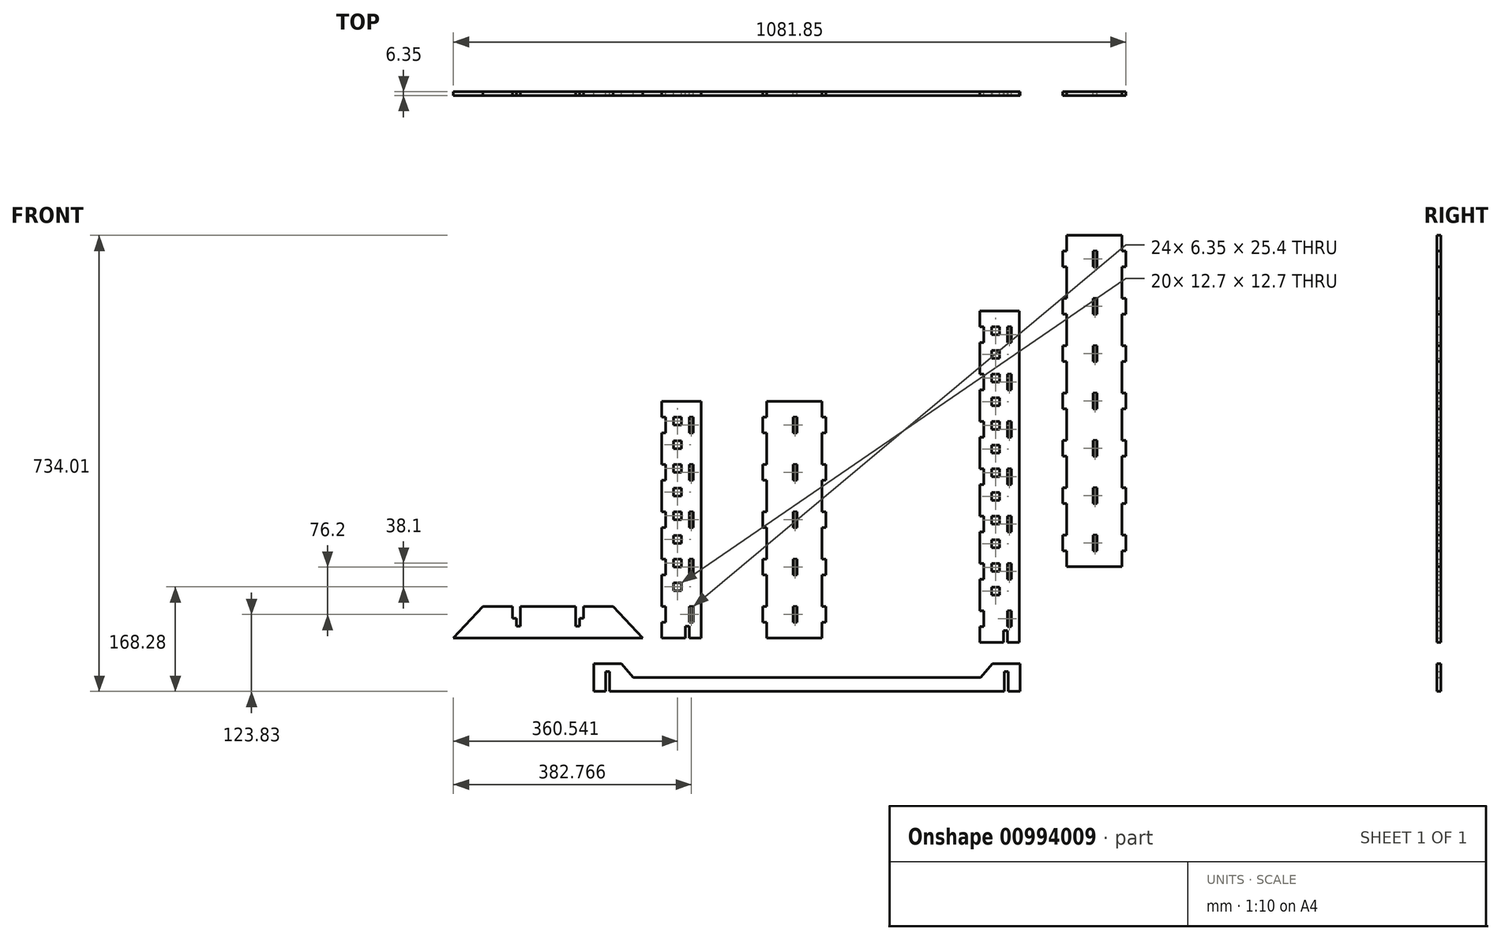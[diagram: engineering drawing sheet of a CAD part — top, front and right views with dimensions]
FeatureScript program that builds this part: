
annotation { "Feature Type Name" : "Feature", "Feature Type Description" : "" }
export const myFeature = defineFeature(function(context is Context, id is Id, definition is map)
    precondition{}
    {
        {
            var Q0;
            Q0=qCreatedBy(makeId("Front.planeOp"),FACE);
            var sketch = newSketch(context, id + "F0", { "sketchPlane" : qUnion([Q0])});
            skLineSegment(sketch, "E0", {"start": v(43.26, 355.6) * mm, "end": v(49.61, 355.6) * mm});
            skLineSegment(sketch, "E1", {"start": v(43.26, 330.2) * mm, "end": v(49.61, 330.2) * mm});
            skLineSegment(sketch, "E2", {"start": v(43.26, 279.4) * mm, "end": v(49.61, 279.4) * mm});
            skLineSegment(sketch, "E3", {"start": v(43.26, 254) * mm, "end": v(49.61, 254) * mm});
            skLineSegment(sketch, "E4", {"start": v(43.26, 203.2) * mm, "end": v(49.61, 203.2) * mm});
            skLineSegment(sketch, "E5", {"start": v(43.26, 177.8) * mm, "end": v(49.61, 177.8) * mm});
            skLineSegment(sketch, "E6", {"start": v(43.26, 127) * mm, "end": v(49.61, 127) * mm});
            skLineSegment(sketch, "E7", {"start": v(43.26, 101.6) * mm, "end": v(49.61, 101.6) * mm});
            skLineSegment(sketch, "E8", {"start": v(43.26, 50.8) * mm, "end": v(49.61, 50.8) * mm});
            skLineSegment(sketch, "E9", {"start": v(43.26, 25.4) * mm, "end": v(49.61, 25.4) * mm});
            skLineSegment(sketch, "E10", {"start": v(43.26, 0) * mm, "end": v(43.26, 25.4) * mm});
            skLineSegment(sketch, "E11", {"start": v(49.61, 25.4) * mm, "end": v(49.61, 50.8) * mm});
            skLineSegment(sketch, "E12", {"start": v(43.26, 50.8) * mm, "end": v(43.26, 101.6) * mm});
            skLineSegment(sketch, "E13", {"start": v(49.61, 101.6) * mm, "end": v(49.61, 127) * mm});
            skLineSegment(sketch, "E14", {"start": v(43.26, 127) * mm, "end": v(43.26, 177.8) * mm});
            skLineSegment(sketch, "E15", {"start": v(49.61, 177.8) * mm, "end": v(49.61, 203.2) * mm});
            skLineSegment(sketch, "E16", {"start": v(43.26, 203.2) * mm, "end": v(43.26, 254) * mm});
            skLineSegment(sketch, "E17", {"start": v(49.61, 254) * mm, "end": v(49.61, 279.4) * mm});
            skLineSegment(sketch, "E18", {"start": v(43.26, 279.4) * mm, "end": v(43.26, 330.2) * mm});
            skLineSegment(sketch, "E19", {"start": v(49.61, 330.2) * mm, "end": v(49.61, 355.6) * mm});
            skLineSegment(sketch, "E20", {"start": v(43.26, 355.6) * mm, "end": v(43.26, 381) * mm});
            skLineSegment(sketch, "E21", {"start": v(-45.64, 0) * mm, "end": v(43.26, 0) * mm});
            skLineSegment(sketch, "E22", {"start": v(-45.64, 381) * mm, "end": v(43.26, 381) * mm});
            skLineSegment(sketch, "E23", {"start": v(-45.64, 25.4) * mm, "end": v(-51.99, 25.4) * mm});
            skLineSegment(sketch, "E24", {"start": v(-45.64, 50.8) * mm, "end": v(-51.99, 50.8) * mm});
            skLineSegment(sketch, "E25", {"start": v(-45.64, 101.6) * mm, "end": v(-51.99, 101.6) * mm});
            skLineSegment(sketch, "E26", {"start": v(-45.64, 127) * mm, "end": v(-51.99, 127) * mm});
            skLineSegment(sketch, "E27", {"start": v(-45.64, 177.8) * mm, "end": v(-51.99, 177.8) * mm});
            skLineSegment(sketch, "E28", {"start": v(-45.64, 203.2) * mm, "end": v(-51.99, 203.2) * mm});
            skLineSegment(sketch, "E29", {"start": v(-45.64, 254) * mm, "end": v(-51.99, 254) * mm});
            skLineSegment(sketch, "E30", {"start": v(-45.64, 279.4) * mm, "end": v(-51.99, 279.4) * mm});
            skLineSegment(sketch, "E31", {"start": v(-45.64, 330.2) * mm, "end": v(-51.99, 330.2) * mm});
            skLineSegment(sketch, "E32", {"start": v(-45.64, 355.6) * mm, "end": v(-51.99, 355.6) * mm});
            skLineSegment(sketch, "E33", {"start": v(-45.64, 381) * mm, "end": v(-45.64, 355.6) * mm});
            skLineSegment(sketch, "E34", {"start": v(-45.64, 330.2) * mm, "end": v(-45.64, 279.4) * mm});
            skLineSegment(sketch, "E35", {"start": v(-51.99, 279.4) * mm, "end": v(-51.99, 254) * mm});
            skLineSegment(sketch, "E36", {"start": v(-45.64, 254) * mm, "end": v(-45.64, 203.2) * mm});
            skLineSegment(sketch, "E37", {"start": v(-51.99, 203.2) * mm, "end": v(-51.99, 177.8) * mm});
            skLineSegment(sketch, "E38", {"start": v(-45.64, 177.8) * mm, "end": v(-45.64, 127) * mm});
            skLineSegment(sketch, "E39", {"start": v(-51.99, 127) * mm, "end": v(-51.99, 101.6) * mm});
            skLineSegment(sketch, "E40", {"start": v(-45.64, 101.6) * mm, "end": v(-45.64, 50.8) * mm});
            skLineSegment(sketch, "E41", {"start": v(-51.99, 50.8) * mm, "end": v(-51.99, 25.4) * mm});
            skLineSegment(sketch, "E42", {"start": v(-45.64, 25.4) * mm, "end": v(-45.64, 0) * mm});
            skLineSegment(sketch, "E43", {"start": v(-51.99, 355.6) * mm, "end": v(-51.99, 330.2) * mm});
            skLineSegment(sketch, "E44", {"start": v(2.99, 25.4) * mm, "end": v(-3.36, 25.4) * mm});
            skLineSegment(sketch, "E45", {"start": v(2.99, 50.8) * mm, "end": v(-3.36, 50.8) * mm});
            skLineSegment(sketch, "E46", {"start": v(2.99, 101.6) * mm, "end": v(-3.36, 101.6) * mm});
            skLineSegment(sketch, "E47", {"start": v(2.99, 127) * mm, "end": v(-3.36, 127) * mm});
            skLineSegment(sketch, "E48", {"start": v(2.99, 177.8) * mm, "end": v(-3.36, 177.8) * mm});
            skLineSegment(sketch, "E49", {"start": v(2.99, 203.2) * mm, "end": v(-3.36, 203.2) * mm});
            skLineSegment(sketch, "E50", {"start": v(2.99, 254) * mm, "end": v(-3.36, 254) * mm});
            skLineSegment(sketch, "E51", {"start": v(2.99, 279.4) * mm, "end": v(-3.36, 279.4) * mm});
            skLineSegment(sketch, "E52", {"start": v(2.99, 330.2) * mm, "end": v(-3.36, 330.2) * mm});
            skLineSegment(sketch, "E53", {"start": v(2.99, 355.6) * mm, "end": v(-3.36, 355.6) * mm});
            skLineSegment(sketch, "E54", {"start": v(-3.36, 279.4) * mm, "end": v(-3.36, 254) * mm});
            skLineSegment(sketch, "E55", {"start": v(-3.36, 203.2) * mm, "end": v(-3.36, 177.8) * mm});
            skLineSegment(sketch, "E56", {"start": v(-3.36, 127) * mm, "end": v(-3.36, 101.6) * mm});
            skLineSegment(sketch, "E57", {"start": v(-3.36, 50.8) * mm, "end": v(-3.36, 25.4) * mm});
            skLineSegment(sketch, "E58", {"start": v(-3.36, 355.6) * mm, "end": v(-3.36, 330.2) * mm});
            skLineSegment(sketch, "E59", {"start": v(2.99, 355.6) * mm, "end": v(2.99, 330.2) * mm});
            skLineSegment(sketch, "E60", {"start": v(2.99, 279.4) * mm, "end": v(2.99, 254) * mm});
            skLineSegment(sketch, "E61", {"start": v(2.99, 203.2) * mm, "end": v(2.99, 177.8) * mm});
            skLineSegment(sketch, "E62", {"start": v(2.99, 127) * mm, "end": v(2.99, 101.6) * mm});
            skLineSegment(sketch, "E63", {"start": v(2.99, 50.8) * mm, "end": v(2.99, 25.4) * mm});
            skSolve(sketch);
        }
        {
            var Q0;
            Q0 = qSketchRegion(id + "F0", true);
            extrude(context, id + "F1", {"entities" : qUnion([Q0]), "depth" : 6.35 * mm, "offsetDistance" : 25.4 * mm});
        }
        {
            var Q0;
            Q0=qCreatedBy(makeId("Front.planeOp"),FACE);
            var sketch = newSketch(context, id + "F2", { "sketchPlane" : qUnion([Q0])});
            skLineSegment(sketch, "E64.top", {"start": v(-151.2, 381) * mm, "end": v(-214.7, 381) * mm});
            skLineSegment(sketch, "E64.left", {"start": v(-151.2, 0) * mm, "end": v(-151.2, 381) * mm});
            skLineSegment(sketch, "E65", {"start": v(-163.9, 25.4) * mm, "end": v(-170.25, 25.4) * mm});
            skLineSegment(sketch, "E66", {"start": v(-163.9, 50.8) * mm, "end": v(-170.25, 50.8) * mm});
            skLineSegment(sketch, "E67", {"start": v(-163.9, 101.6) * mm, "end": v(-170.25, 101.6) * mm});
            skLineSegment(sketch, "E68", {"start": v(-163.9, 127) * mm, "end": v(-170.25, 127) * mm});
            skLineSegment(sketch, "E69", {"start": v(-163.9, 177.8) * mm, "end": v(-170.25, 177.8) * mm});
            skLineSegment(sketch, "E70", {"start": v(-163.9, 203.2) * mm, "end": v(-170.25, 203.2) * mm});
            skLineSegment(sketch, "E71", {"start": v(-163.9, 254) * mm, "end": v(-170.25, 254) * mm});
            skLineSegment(sketch, "E72", {"start": v(-163.9, 279.4) * mm, "end": v(-170.25, 279.4) * mm});
            skLineSegment(sketch, "E73", {"start": v(-163.9, 330.2) * mm, "end": v(-170.25, 330.2) * mm});
            skLineSegment(sketch, "E74", {"start": v(-163.9, 355.6) * mm, "end": v(-170.25, 355.6) * mm});
            skLineSegment(sketch, "E75", {"start": v(-170.25, 279.4) * mm, "end": v(-170.25, 254) * mm});
            skLineSegment(sketch, "E76", {"start": v(-170.25, 203.2) * mm, "end": v(-170.25, 177.8) * mm});
            skLineSegment(sketch, "E77", {"start": v(-170.25, 127) * mm, "end": v(-170.25, 101.6) * mm});
            skLineSegment(sketch, "E78", {"start": v(-170.25, 355.6) * mm, "end": v(-170.25, 330.2) * mm});
            skLineSegment(sketch, "E79", {"start": v(-163.9, 355.6) * mm, "end": v(-163.9, 330.2) * mm});
            skLineSegment(sketch, "E80", {"start": v(-163.9, 279.4) * mm, "end": v(-163.9, 254) * mm});
            skLineSegment(sketch, "E81", {"start": v(-163.9, 203.2) * mm, "end": v(-163.9, 177.8) * mm});
            skLineSegment(sketch, "E82", {"start": v(-163.9, 127) * mm, "end": v(-163.9, 101.6) * mm});
            skLineSegment(sketch, "E83", {"start": v(-163.9, 50.8) * mm, "end": v(-163.9, 25.4) * mm});
            skLineSegment(sketch, "E84", {"start": v(-208.35, 25.4) * mm, "end": v(-214.7, 25.4) * mm});
            skLineSegment(sketch, "E85", {"start": v(-208.35, 50.8) * mm, "end": v(-214.7, 50.8) * mm});
            skLineSegment(sketch, "E86", {"start": v(-208.35, 101.6) * mm, "end": v(-214.7, 101.6) * mm});
            skLineSegment(sketch, "E87", {"start": v(-208.35, 127) * mm, "end": v(-214.7, 127) * mm});
            skLineSegment(sketch, "E88", {"start": v(-208.35, 177.8) * mm, "end": v(-214.7, 177.8) * mm});
            skLineSegment(sketch, "E89", {"start": v(-208.35, 203.2) * mm, "end": v(-214.7, 203.2) * mm});
            skLineSegment(sketch, "E90", {"start": v(-208.35, 254) * mm, "end": v(-214.7, 254) * mm});
            skLineSegment(sketch, "E91", {"start": v(-208.35, 279.4) * mm, "end": v(-214.7, 279.4) * mm});
            skLineSegment(sketch, "E92", {"start": v(-208.35, 330.2) * mm, "end": v(-214.7, 330.2) * mm});
            skLineSegment(sketch, "E93", {"start": v(-208.35, 355.6) * mm, "end": v(-214.7, 355.6) * mm});
            skLineSegment(sketch, "E94", {"start": v(-208.35, 355.6) * mm, "end": v(-208.35, 330.2) * mm});
            skLineSegment(sketch, "E95", {"start": v(-208.35, 279.4) * mm, "end": v(-208.35, 254) * mm});
            skLineSegment(sketch, "E96", {"start": v(-208.35, 203.2) * mm, "end": v(-208.35, 177.8) * mm});
            skLineSegment(sketch, "E97", {"start": v(-208.35, 127) * mm, "end": v(-208.35, 101.6) * mm});
            skLineSegment(sketch, "E98", {"start": v(-208.35, 50.8) * mm, "end": v(-208.35, 25.4) * mm});
            skLineSegment(sketch, "E99", {"start": v(-214.7, 0) * mm, "end": v(-214.7, 25.4) * mm});
            skLineSegment(sketch, "E100", {"start": v(-214.7, 50.8) * mm, "end": v(-214.7, 101.6) * mm});
            skLineSegment(sketch, "E101", {"start": v(-214.7, 127) * mm, "end": v(-214.7, 177.8) * mm});
            skLineSegment(sketch, "E102", {"start": v(-214.7, 203.2) * mm, "end": v(-214.7, 254) * mm});
            skLineSegment(sketch, "E103", {"start": v(-214.7, 279.4) * mm, "end": v(-214.7, 330.2) * mm});
            skLineSegment(sketch, "E104", {"start": v(-214.7, 355.6) * mm, "end": v(-214.7, 381) * mm});
            skLineSegment(sketch, "E105", {"start": v(-214.7, 0) * mm, "end": v(-182.95, 0) * mm});
            skLineSegment(sketch, "E106", {"start": v(-170.25, 25.4) * mm, "end": v(-170.25, 50.8) * mm});
            skLineSegment(sketch, "E107", {"start": v(-170.25, 0) * mm, "end": v(-170.25, 19.05) * mm});
            skLineSegment(sketch, "E108", {"start": v(-170.25, 19.05) * mm, "end": v(-176.6, 19.05) * mm});
            skLineSegment(sketch, "E109", {"start": v(-176.6, 19.05) * mm, "end": v(-176.6, 0) * mm});
            skLineSegment(sketch, "E110.bottom", {"start": v(-195.65, 76.2) * mm, "end": v(-182.95, 76.2) * mm});
            skLineSegment(sketch, "E110.top", {"start": v(-195.65, 88.9) * mm, "end": v(-182.95, 88.9) * mm});
            skLineSegment(sketch, "E110.left", {"start": v(-195.65, 76.2) * mm, "end": v(-195.65, 88.9) * mm});
            skLineSegment(sketch, "E110.right", {"start": v(-182.95, 76.2) * mm, "end": v(-182.95, 88.9) * mm});
            skLineSegment(sketch, "E111.bottom", {"start": v(-195.65, 114.3) * mm, "end": v(-182.95, 114.3) * mm});
            skLineSegment(sketch, "E111.top", {"start": v(-195.65, 127) * mm, "end": v(-182.95, 127) * mm});
            skLineSegment(sketch, "E111.left", {"start": v(-195.65, 114.3) * mm, "end": v(-195.65, 127) * mm});
            skLineSegment(sketch, "E111.right", {"start": v(-182.95, 114.3) * mm, "end": v(-182.95, 127) * mm});
            skLineSegment(sketch, "E112.bottom", {"start": v(-195.65, 152.4) * mm, "end": v(-182.95, 152.4) * mm});
            skLineSegment(sketch, "E112.top", {"start": v(-195.65, 165.1) * mm, "end": v(-182.95, 165.1) * mm});
            skLineSegment(sketch, "E112.left", {"start": v(-195.65, 152.4) * mm, "end": v(-195.65, 165.1) * mm});
            skLineSegment(sketch, "E112.right", {"start": v(-182.95, 152.4) * mm, "end": v(-182.95, 165.1) * mm});
            skLineSegment(sketch, "E113.bottom", {"start": v(-195.65, 190.5) * mm, "end": v(-182.95, 190.5) * mm});
            skLineSegment(sketch, "E113.top", {"start": v(-195.65, 203.2) * mm, "end": v(-182.95, 203.2) * mm});
            skLineSegment(sketch, "E113.left", {"start": v(-195.65, 190.5) * mm, "end": v(-195.65, 203.2) * mm});
            skLineSegment(sketch, "E113.right", {"start": v(-182.95, 190.5) * mm, "end": v(-182.95, 203.2) * mm});
            skLineSegment(sketch, "E114.bottom", {"start": v(-195.65, 228.6) * mm, "end": v(-182.95, 228.6) * mm});
            skLineSegment(sketch, "E114.top", {"start": v(-195.65, 241.3) * mm, "end": v(-182.95, 241.3) * mm});
            skLineSegment(sketch, "E114.left", {"start": v(-195.65, 228.6) * mm, "end": v(-195.65, 241.3) * mm});
            skLineSegment(sketch, "E114.right", {"start": v(-182.95, 228.6) * mm, "end": v(-182.95, 241.3) * mm});
            skLineSegment(sketch, "E115.bottom", {"start": v(-195.65, 266.7) * mm, "end": v(-182.95, 266.7) * mm});
            skLineSegment(sketch, "E115.top", {"start": v(-195.65, 279.4) * mm, "end": v(-182.95, 279.4) * mm});
            skLineSegment(sketch, "E115.left", {"start": v(-195.65, 266.7) * mm, "end": v(-195.65, 279.4) * mm});
            skLineSegment(sketch, "E115.right", {"start": v(-182.95, 266.7) * mm, "end": v(-182.95, 279.4) * mm});
            skLineSegment(sketch, "E116.bottom", {"start": v(-195.65, 304.8) * mm, "end": v(-182.95, 304.8) * mm});
            skLineSegment(sketch, "E116.top", {"start": v(-195.65, 317.5) * mm, "end": v(-182.95, 317.5) * mm});
            skLineSegment(sketch, "E116.left", {"start": v(-195.65, 304.8) * mm, "end": v(-195.65, 317.5) * mm});
            skLineSegment(sketch, "E116.right", {"start": v(-182.95, 304.8) * mm, "end": v(-182.95, 317.5) * mm});
            skLineSegment(sketch, "E117.bottom", {"start": v(-195.65, 342.9) * mm, "end": v(-182.95, 342.9) * mm});
            skLineSegment(sketch, "E117.top", {"start": v(-195.65, 355.6) * mm, "end": v(-182.95, 355.6) * mm});
            skLineSegment(sketch, "E117.left", {"start": v(-195.65, 342.9) * mm, "end": v(-195.65, 355.6) * mm});
            skLineSegment(sketch, "E117.right", {"start": v(-182.95, 342.9) * mm, "end": v(-182.95, 355.6) * mm});
            skLineSegment(sketch, "E118", {"start": v(-170.25, 0) * mm, "end": v(-151.2, 0) * mm});
            skLineSegment(sketch, "E119", {"start": v(-176.6, 0) * mm, "end": v(-182.95, 0) * mm});
            skSolve(sketch);
        }
        {
            var Q0;
            Q0=makeQuery(id+"F2.imprint","IMPRINT",FACE,{"disambiguationData":[TD([[makeQuery(id+"F2.imprint","IMPRINT",EDGE,{"derivedFrom":sQuery(id+"F2.wireOp",EDGE,"E64.top")}),1.0]])]});
            extrude(context, id + "F3", {"entities" : qUnion([Q0]), "depth" : 6.35 * mm, "offsetDistance" : 25.4 * mm});
        }
        {
            var Q0;
            Q0=qCreatedBy(makeId("Front.planeOp"),FACE);
            var sketch = newSketch(context, id + "F4", { "sketchPlane" : qUnion([Q0])});
            skLineSegment(sketch, "E120.bottom", {"start": v(-245.04, 0) * mm, "end": v(-549.84, 0) * mm});
            skLineSegment(sketch, "E121.bottom", {"start": v(-441.89, 50.8) * mm, "end": v(-352.99, 50.8) * mm});
            skLineSegment(sketch, "E121.left", {"start": v(-441.89, 50.8) * mm, "end": v(-441.89, 19.05) * mm});
            skLineSegment(sketch, "E121.right", {"start": v(-352.99, 50.8) * mm, "end": v(-352.99, 19.05) * mm});
            skLineSegment(sketch, "E122", {"start": v(-448.24, 19.05) * mm, "end": v(-448.24, 31.75) * mm});
            skLineSegment(sketch, "E123", {"start": v(-448.24, 31.75) * mm, "end": v(-454.59, 31.75) * mm});
            skLineSegment(sketch, "E124", {"start": v(-454.59, 50.8) * mm, "end": v(-454.59, 31.75) * mm});
            skLineSegment(sketch, "E125", {"start": v(-448.24, 19.05) * mm, "end": v(-441.89, 19.05) * mm});
            skLineSegment(sketch, "E126", {"start": v(-346.64, 19.05) * mm, "end": v(-346.64, 31.75) * mm});
            skLineSegment(sketch, "E127", {"start": v(-346.64, 31.75) * mm, "end": v(-340.29, 31.75) * mm});
            skLineSegment(sketch, "E128", {"start": v(-340.29, 31.75) * mm, "end": v(-340.29, 50.8) * mm});
            skLineSegment(sketch, "E129", {"start": v(-346.64, 19.05) * mm, "end": v(-352.99, 19.05) * mm});
            skLineSegment(sketch, "E130", {"start": v(-454.59, 50.8) * mm, "end": v(-502.21, 50.8) * mm});
            skLineSegment(sketch, "E131", {"start": v(-549.84, 0) * mm, "end": v(-502.21, 50.8) * mm});
            skLineSegment(sketch, "E132", {"start": v(-340.29, 50.8) * mm, "end": v(-292.66, 50.8) * mm});
            skLineSegment(sketch, "E133", {"start": v(-245.04, 0) * mm, "end": v(-292.66, 50.8) * mm});
            skSolve(sketch);
        }
        {
            var Q0;
            Q0=makeQuery(id+"F4.imprint","IMPRINT",FACE,{"disambiguationData":[TD([[makeQuery(id+"F4.imprint","IMPRINT",EDGE,{"derivedFrom":sQuery(id+"F4.wireOp",EDGE,"E120.bottom")}),-1.0]])]});
            extrude(context, id + "F5", {"entities" : qUnion([Q0]), "depth" : 6.35 * mm, "offsetDistance" : 25.4 * mm});
        }
        {
            var Q0;
            Q0=qCreatedBy(makeId("Front.planeOp"),FACE);
            var sketch = newSketch(context, id + "F6", { "sketchPlane" : qUnion([Q0])});
            skLineSegment(sketch, "E134", {"start": v(-324.25, -85.73) * mm, "end": v(-305.2, -85.73) * mm});
            skLineSegment(sketch, "E135", {"start": v(-305.2, -85.73) * mm, "end": v(-305.2, -53.98) * mm});
            skLineSegment(sketch, "E136", {"start": v(-305.2, -53.98) * mm, "end": v(-298.85, -53.98) * mm});
            skLineSegment(sketch, "E137", {"start": v(-298.85, -53.98) * mm, "end": v(-298.85, -85.73) * mm});
            skLineSegment(sketch, "E138", {"start": v(361.55, -85.73) * mm, "end": v(342.5, -85.73) * mm});
            skLineSegment(sketch, "E139", {"start": v(342.5, -85.73) * mm, "end": v(342.5, -53.98) * mm});
            skLineSegment(sketch, "E140", {"start": v(342.5, -53.98) * mm, "end": v(336.15, -53.98) * mm});
            skLineSegment(sketch, "E141", {"start": v(336.15, -53.98) * mm, "end": v(336.15, -85.73) * mm});
            skLineSegment(sketch, "E142", {"start": v(336.15, -85.73) * mm, "end": v(-298.85, -85.73) * mm});
            skLineSegment(sketch, "E143", {"start": v(-324.25, -85.73) * mm, "end": v(-324.25, -41.28) * mm});
            skLineSegment(sketch, "E144", {"start": v(361.55, -85.73) * mm, "end": v(361.55, -41.28) * mm});
            skLineSegment(sketch, "E145", {"start": v(-324.25, -41.28) * mm, "end": v(-279.8, -41.28) * mm});
            skLineSegment(sketch, "E146", {"start": v(361.55, -41.28) * mm, "end": v(317.1, -41.28) * mm});
            skLineSegment(sketch, "E147", {"start": v(-279.8, -41.28) * mm, "end": v(-260.75, -63.5) * mm});
            skLineSegment(sketch, "E148", {"start": v(298.05, -63.5) * mm, "end": v(317.1, -41.28) * mm});
            skLineSegment(sketch, "E149", {"start": v(-260.75, -63.5) * mm, "end": v(298.05, -63.5) * mm});
            skSolve(sketch);
        }
        {
            var Q0;
            Q0=makeQuery(id+"F6.imprint","IMPRINT",FACE,{"disambiguationData":[TD([[makeQuery(id+"F6.imprint","IMPRINT",EDGE,{"derivedFrom":sQuery(id+"F6.wireOp",EDGE,"E134")}),1.0]])]});
            extrude(context, id + "F7", {"entities" : qUnion([Q0]), "depth" : 6.35 * mm, "offsetDistance" : 25.4 * mm});
        }
        {
            var Q0;
            Q0=qCreatedBy(makeId("Front.planeOp"),FACE);
            var sketch = newSketch(context, id + "F8", { "sketchPlane" : qUnion([Q0])});
            skLineSegment(sketch, "E150", {"start": v(525.66, 470.48) * mm, "end": v(532, 470.48) * mm});
            skLineSegment(sketch, "E151", {"start": v(525.66, 445.08) * mm, "end": v(532, 445.08) * mm});
            skLineSegment(sketch, "E152", {"start": v(525.66, 394.28) * mm, "end": v(532, 394.28) * mm});
            skLineSegment(sketch, "E153", {"start": v(525.66, 368.88) * mm, "end": v(532, 368.88) * mm});
            skLineSegment(sketch, "E154", {"start": v(525.66, 318.08) * mm, "end": v(532, 318.08) * mm});
            skLineSegment(sketch, "E155", {"start": v(525.66, 292.68) * mm, "end": v(532, 292.68) * mm});
            skLineSegment(sketch, "E156", {"start": v(525.66, 241.88) * mm, "end": v(532, 241.88) * mm});
            skLineSegment(sketch, "E157", {"start": v(525.66, 216.48) * mm, "end": v(532, 216.48) * mm});
            skLineSegment(sketch, "E158", {"start": v(525.66, 165.68) * mm, "end": v(532, 165.68) * mm});
            skLineSegment(sketch, "E159", {"start": v(525.66, 140.28) * mm, "end": v(532, 140.28) * mm});
            skLineSegment(sketch, "E160", {"start": v(525.66, 114.88) * mm, "end": v(525.66, 140.28) * mm});
            skLineSegment(sketch, "E161", {"start": v(532, 140.28) * mm, "end": v(532, 165.68) * mm});
            skLineSegment(sketch, "E162", {"start": v(525.66, 165.68) * mm, "end": v(525.66, 216.48) * mm});
            skLineSegment(sketch, "E163", {"start": v(532, 216.48) * mm, "end": v(532, 241.88) * mm});
            skLineSegment(sketch, "E164", {"start": v(525.66, 241.88) * mm, "end": v(525.66, 292.68) * mm});
            skLineSegment(sketch, "E165", {"start": v(532, 292.68) * mm, "end": v(532, 318.08) * mm});
            skLineSegment(sketch, "E166", {"start": v(525.66, 318.08) * mm, "end": v(525.66, 368.88) * mm});
            skLineSegment(sketch, "E167", {"start": v(532, 368.88) * mm, "end": v(532, 394.28) * mm});
            skLineSegment(sketch, "E168", {"start": v(525.66, 394.28) * mm, "end": v(525.66, 445.08) * mm});
            skLineSegment(sketch, "E169", {"start": v(532, 445.08) * mm, "end": v(532, 470.48) * mm});
            skLineSegment(sketch, "E170", {"start": v(436.76, 114.88) * mm, "end": v(525.66, 114.88) * mm});
            skLineSegment(sketch, "E171", {"start": v(436.76, 140.28) * mm, "end": v(430.4, 140.28) * mm});
            skLineSegment(sketch, "E172", {"start": v(436.76, 165.68) * mm, "end": v(430.4, 165.68) * mm});
            skLineSegment(sketch, "E173", {"start": v(436.76, 216.48) * mm, "end": v(430.4, 216.48) * mm});
            skLineSegment(sketch, "E174", {"start": v(436.76, 241.88) * mm, "end": v(430.4, 241.88) * mm});
            skLineSegment(sketch, "E175", {"start": v(436.76, 292.68) * mm, "end": v(430.4, 292.68) * mm});
            skLineSegment(sketch, "E176", {"start": v(436.76, 318.08) * mm, "end": v(430.4, 318.08) * mm});
            skLineSegment(sketch, "E177", {"start": v(436.76, 368.88) * mm, "end": v(430.4, 368.88) * mm});
            skLineSegment(sketch, "E178", {"start": v(436.76, 394.28) * mm, "end": v(430.4, 394.28) * mm});
            skLineSegment(sketch, "E179", {"start": v(436.76, 445.08) * mm, "end": v(430.4, 445.08) * mm});
            skLineSegment(sketch, "E180", {"start": v(436.76, 470.48) * mm, "end": v(430.4, 470.48) * mm});
            skLineSegment(sketch, "E181", {"start": v(436.76, 445.08) * mm, "end": v(436.76, 394.28) * mm});
            skLineSegment(sketch, "E182", {"start": v(430.4, 394.28) * mm, "end": v(430.4, 368.88) * mm});
            skLineSegment(sketch, "E183", {"start": v(436.76, 368.88) * mm, "end": v(436.76, 318.08) * mm});
            skLineSegment(sketch, "E184", {"start": v(430.4, 318.08) * mm, "end": v(430.4, 292.68) * mm});
            skLineSegment(sketch, "E185", {"start": v(436.76, 292.68) * mm, "end": v(436.76, 241.88) * mm});
            skLineSegment(sketch, "E186", {"start": v(430.4, 241.88) * mm, "end": v(430.4, 216.48) * mm});
            skLineSegment(sketch, "E187", {"start": v(436.76, 216.48) * mm, "end": v(436.76, 165.68) * mm});
            skLineSegment(sketch, "E188", {"start": v(430.4, 165.68) * mm, "end": v(430.4, 140.28) * mm});
            skLineSegment(sketch, "E189", {"start": v(436.76, 140.28) * mm, "end": v(436.76, 114.88) * mm});
            skLineSegment(sketch, "E190", {"start": v(430.4, 470.48) * mm, "end": v(430.4, 445.08) * mm});
            skLineSegment(sketch, "E191", {"start": v(485.38, 140.28) * mm, "end": v(479.03, 140.28) * mm});
            skLineSegment(sketch, "E192", {"start": v(485.38, 165.68) * mm, "end": v(479.03, 165.68) * mm});
            skLineSegment(sketch, "E193", {"start": v(485.38, 216.48) * mm, "end": v(479.03, 216.48) * mm});
            skLineSegment(sketch, "E194", {"start": v(485.38, 241.88) * mm, "end": v(479.03, 241.88) * mm});
            skLineSegment(sketch, "E195", {"start": v(485.38, 292.68) * mm, "end": v(479.03, 292.68) * mm});
            skLineSegment(sketch, "E196", {"start": v(485.38, 318.08) * mm, "end": v(479.03, 318.08) * mm});
            skLineSegment(sketch, "E197", {"start": v(485.38, 368.88) * mm, "end": v(479.03, 368.88) * mm});
            skLineSegment(sketch, "E198", {"start": v(485.38, 394.28) * mm, "end": v(479.03, 394.28) * mm});
            skLineSegment(sketch, "E199", {"start": v(485.38, 445.08) * mm, "end": v(479.03, 445.08) * mm});
            skLineSegment(sketch, "E200", {"start": v(485.38, 470.48) * mm, "end": v(479.03, 470.48) * mm});
            skLineSegment(sketch, "E201", {"start": v(479.03, 394.28) * mm, "end": v(479.03, 368.88) * mm});
            skLineSegment(sketch, "E202", {"start": v(479.03, 318.08) * mm, "end": v(479.03, 292.68) * mm});
            skLineSegment(sketch, "E203", {"start": v(479.03, 241.88) * mm, "end": v(479.03, 216.48) * mm});
            skLineSegment(sketch, "E204", {"start": v(479.03, 165.68) * mm, "end": v(479.03, 140.28) * mm});
            skLineSegment(sketch, "E205", {"start": v(479.03, 470.48) * mm, "end": v(479.03, 445.08) * mm});
            skLineSegment(sketch, "E206", {"start": v(485.38, 470.48) * mm, "end": v(485.38, 445.08) * mm});
            skLineSegment(sketch, "E207", {"start": v(485.38, 394.28) * mm, "end": v(485.38, 368.88) * mm});
            skLineSegment(sketch, "E208", {"start": v(485.38, 318.08) * mm, "end": v(485.38, 292.68) * mm});
            skLineSegment(sketch, "E209", {"start": v(485.38, 241.88) * mm, "end": v(485.38, 216.48) * mm});
            skLineSegment(sketch, "E210", {"start": v(485.38, 165.68) * mm, "end": v(485.38, 140.28) * mm});
            skLineSegment(sketch, "E211", {"start": v(525.66, 622.88) * mm, "end": v(532, 622.88) * mm});
            skLineSegment(sketch, "E212", {"start": v(525.66, 597.48) * mm, "end": v(532, 597.48) * mm});
            skLineSegment(sketch, "E213", {"start": v(525.66, 546.68) * mm, "end": v(532, 546.68) * mm});
            skLineSegment(sketch, "E214", {"start": v(525.66, 521.28) * mm, "end": v(532, 521.28) * mm});
            skLineSegment(sketch, "E215", {"start": v(525.66, 470.48) * mm, "end": v(525.66, 521.28) * mm});
            skLineSegment(sketch, "E216", {"start": v(532, 521.28) * mm, "end": v(532, 546.68) * mm});
            skLineSegment(sketch, "E217", {"start": v(525.66, 546.68) * mm, "end": v(525.66, 597.48) * mm});
            skLineSegment(sketch, "E218", {"start": v(532, 597.48) * mm, "end": v(532, 622.88) * mm});
            skLineSegment(sketch, "E219", {"start": v(436.76, 521.28) * mm, "end": v(430.4, 521.28) * mm});
            skLineSegment(sketch, "E220", {"start": v(436.76, 546.68) * mm, "end": v(430.4, 546.68) * mm});
            skLineSegment(sketch, "E221", {"start": v(436.76, 597.48) * mm, "end": v(430.4, 597.48) * mm});
            skLineSegment(sketch, "E222", {"start": v(436.76, 622.88) * mm, "end": v(430.4, 622.88) * mm});
            skLineSegment(sketch, "E223", {"start": v(436.76, 597.48) * mm, "end": v(436.76, 546.68) * mm});
            skLineSegment(sketch, "E224", {"start": v(430.4, 546.68) * mm, "end": v(430.4, 521.28) * mm});
            skLineSegment(sketch, "E225", {"start": v(436.76, 521.28) * mm, "end": v(436.76, 470.48) * mm});
            skLineSegment(sketch, "E226", {"start": v(430.4, 622.88) * mm, "end": v(430.4, 597.48) * mm});
            skLineSegment(sketch, "E227", {"start": v(485.38, 521.28) * mm, "end": v(479.03, 521.28) * mm});
            skLineSegment(sketch, "E228", {"start": v(485.38, 546.68) * mm, "end": v(479.03, 546.68) * mm});
            skLineSegment(sketch, "E229", {"start": v(485.38, 597.48) * mm, "end": v(479.03, 597.48) * mm});
            skLineSegment(sketch, "E230", {"start": v(485.38, 622.88) * mm, "end": v(479.03, 622.88) * mm});
            skLineSegment(sketch, "E231", {"start": v(479.03, 546.68) * mm, "end": v(479.03, 521.28) * mm});
            skLineSegment(sketch, "E232", {"start": v(479.03, 622.88) * mm, "end": v(479.03, 597.48) * mm});
            skLineSegment(sketch, "E233", {"start": v(485.38, 622.88) * mm, "end": v(485.38, 597.48) * mm});
            skLineSegment(sketch, "E234", {"start": v(485.38, 546.68) * mm, "end": v(485.38, 521.28) * mm});
            skLineSegment(sketch, "E235", {"start": v(436.76, 648.28) * mm, "end": v(436.76, 622.88) * mm});
            skLineSegment(sketch, "E236", {"start": v(525.66, 648.28) * mm, "end": v(436.76, 648.28) * mm});
            skLineSegment(sketch, "E237", {"start": v(525.66, 622.88) * mm, "end": v(525.66, 648.28) * mm});
            skSolve(sketch);
        }
        {
            var Q0;
            Q0 = qSketchRegion(id + "F8", true);
            extrude(context, id + "F9", {"entities" : qUnion([Q0]), "depth" : 6.35 * mm, "offsetDistance" : 25.4 * mm});
        }
        {
            var Q0;
            Q0=qCreatedBy(makeId("Front.planeOp"),FACE);
            var sketch = newSketch(context, id + "F10", { "sketchPlane" : qUnion([Q0])});
            skLineSegment(sketch, "E238", {"start": v(347.56, 18.35) * mm, "end": v(341.2, 18.35) * mm});
            skLineSegment(sketch, "E239", {"start": v(347.56, 43.75) * mm, "end": v(341.2, 43.75) * mm});
            skLineSegment(sketch, "E240", {"start": v(347.56, 94.55) * mm, "end": v(341.2, 94.55) * mm});
            skLineSegment(sketch, "E241", {"start": v(347.56, 119.95) * mm, "end": v(341.2, 119.95) * mm});
            skLineSegment(sketch, "E242", {"start": v(347.56, 170.75) * mm, "end": v(341.2, 170.75) * mm});
            skLineSegment(sketch, "E243", {"start": v(347.56, 196.15) * mm, "end": v(341.2, 196.15) * mm});
            skLineSegment(sketch, "E244", {"start": v(347.56, 246.95) * mm, "end": v(341.2, 246.95) * mm});
            skLineSegment(sketch, "E245", {"start": v(347.56, 272.35) * mm, "end": v(341.2, 272.35) * mm});
            skLineSegment(sketch, "E246", {"start": v(347.56, 323.15) * mm, "end": v(341.2, 323.15) * mm});
            skLineSegment(sketch, "E247", {"start": v(347.56, 348.55) * mm, "end": v(341.2, 348.55) * mm});
            skLineSegment(sketch, "E248", {"start": v(341.2, 272.35) * mm, "end": v(341.2, 246.95) * mm});
            skLineSegment(sketch, "E249", {"start": v(341.2, 196.15) * mm, "end": v(341.2, 170.75) * mm});
            skLineSegment(sketch, "E250", {"start": v(341.2, 119.95) * mm, "end": v(341.2, 94.55) * mm});
            skLineSegment(sketch, "E251", {"start": v(341.2, 348.55) * mm, "end": v(341.2, 323.15) * mm});
            skLineSegment(sketch, "E252", {"start": v(347.56, 348.55) * mm, "end": v(347.56, 323.15) * mm});
            skLineSegment(sketch, "E253", {"start": v(347.56, 272.35) * mm, "end": v(347.56, 246.95) * mm});
            skLineSegment(sketch, "E254", {"start": v(347.56, 196.15) * mm, "end": v(347.56, 170.75) * mm});
            skLineSegment(sketch, "E255", {"start": v(347.56, 119.95) * mm, "end": v(347.56, 94.55) * mm});
            skLineSegment(sketch, "E256", {"start": v(347.56, 43.75) * mm, "end": v(347.56, 18.35) * mm});
            skLineSegment(sketch, "E257", {"start": v(303.1, 18.35) * mm, "end": v(296.76, 18.35) * mm});
            skLineSegment(sketch, "E258", {"start": v(303.1, 43.75) * mm, "end": v(296.76, 43.75) * mm});
            skLineSegment(sketch, "E259", {"start": v(303.1, 94.55) * mm, "end": v(296.76, 94.55) * mm});
            skLineSegment(sketch, "E260", {"start": v(303.1, 119.95) * mm, "end": v(296.76, 119.95) * mm});
            skLineSegment(sketch, "E261", {"start": v(303.1, 170.75) * mm, "end": v(296.76, 170.75) * mm});
            skLineSegment(sketch, "E262", {"start": v(303.1, 196.15) * mm, "end": v(296.76, 196.15) * mm});
            skLineSegment(sketch, "E263", {"start": v(303.1, 246.95) * mm, "end": v(296.76, 246.95) * mm});
            skLineSegment(sketch, "E264", {"start": v(303.1, 272.35) * mm, "end": v(296.76, 272.35) * mm});
            skLineSegment(sketch, "E265", {"start": v(303.1, 323.15) * mm, "end": v(296.76, 323.15) * mm});
            skLineSegment(sketch, "E266", {"start": v(303.1, 348.55) * mm, "end": v(296.76, 348.55) * mm});
            skLineSegment(sketch, "E267", {"start": v(303.1, 348.55) * mm, "end": v(303.1, 323.15) * mm});
            skLineSegment(sketch, "E268", {"start": v(303.1, 272.35) * mm, "end": v(303.1, 246.95) * mm});
            skLineSegment(sketch, "E269", {"start": v(303.1, 196.15) * mm, "end": v(303.1, 170.75) * mm});
            skLineSegment(sketch, "E270", {"start": v(303.1, 119.95) * mm, "end": v(303.1, 94.55) * mm});
            skLineSegment(sketch, "E271", {"start": v(303.1, 43.75) * mm, "end": v(303.1, 18.35) * mm});
            skLineSegment(sketch, "E272", {"start": v(296.76, -7.05) * mm, "end": v(296.76, 18.35) * mm});
            skLineSegment(sketch, "E273", {"start": v(296.76, 43.75) * mm, "end": v(296.76, 94.55) * mm});
            skLineSegment(sketch, "E274", {"start": v(296.76, 119.95) * mm, "end": v(296.76, 170.75) * mm});
            skLineSegment(sketch, "E275", {"start": v(296.76, 196.15) * mm, "end": v(296.76, 246.95) * mm});
            skLineSegment(sketch, "E276", {"start": v(296.76, 272.35) * mm, "end": v(296.76, 323.15) * mm});
            skLineSegment(sketch, "E277", {"start": v(296.76, -7.05) * mm, "end": v(328.5, -7.05) * mm});
            skLineSegment(sketch, "E278", {"start": v(341.2, 18.35) * mm, "end": v(341.2, 43.75) * mm});
            skLineSegment(sketch, "E279", {"start": v(341.2, -7.05) * mm, "end": v(341.2, 12) * mm});
            skLineSegment(sketch, "E280", {"start": v(341.2, 12) * mm, "end": v(334.86, 12) * mm});
            skLineSegment(sketch, "E281", {"start": v(334.86, 12) * mm, "end": v(334.86, -7.05) * mm});
            skLineSegment(sketch, "E282.bottom", {"start": v(315.8, 69.15) * mm, "end": v(328.5, 69.15) * mm});
            skLineSegment(sketch, "E282.top", {"start": v(315.8, 81.85) * mm, "end": v(328.5, 81.85) * mm});
            skLineSegment(sketch, "E282.left", {"start": v(315.8, 69.15) * mm, "end": v(315.8, 81.85) * mm});
            skLineSegment(sketch, "E282.right", {"start": v(328.5, 69.15) * mm, "end": v(328.5, 81.85) * mm});
            skLineSegment(sketch, "E283.bottom", {"start": v(315.8, 107.25) * mm, "end": v(328.5, 107.25) * mm});
            skLineSegment(sketch, "E283.top", {"start": v(315.8, 119.95) * mm, "end": v(328.5, 119.95) * mm});
            skLineSegment(sketch, "E283.left", {"start": v(315.8, 107.25) * mm, "end": v(315.8, 119.95) * mm});
            skLineSegment(sketch, "E283.right", {"start": v(328.5, 107.25) * mm, "end": v(328.5, 119.95) * mm});
            skLineSegment(sketch, "E284.bottom", {"start": v(315.8, 145.35) * mm, "end": v(328.5, 145.35) * mm});
            skLineSegment(sketch, "E284.top", {"start": v(315.8, 158.05) * mm, "end": v(328.5, 158.05) * mm});
            skLineSegment(sketch, "E284.left", {"start": v(315.8, 145.35) * mm, "end": v(315.8, 158.05) * mm});
            skLineSegment(sketch, "E284.right", {"start": v(328.5, 145.35) * mm, "end": v(328.5, 158.05) * mm});
            skLineSegment(sketch, "E285.bottom", {"start": v(315.8, 183.45) * mm, "end": v(328.5, 183.45) * mm});
            skLineSegment(sketch, "E285.top", {"start": v(315.8, 196.15) * mm, "end": v(328.5, 196.15) * mm});
            skLineSegment(sketch, "E285.left", {"start": v(315.8, 183.45) * mm, "end": v(315.8, 196.15) * mm});
            skLineSegment(sketch, "E285.right", {"start": v(328.5, 183.45) * mm, "end": v(328.5, 196.15) * mm});
            skLineSegment(sketch, "E286.bottom", {"start": v(315.8, 221.55) * mm, "end": v(328.5, 221.55) * mm});
            skLineSegment(sketch, "E286.top", {"start": v(315.8, 234.25) * mm, "end": v(328.5, 234.25) * mm});
            skLineSegment(sketch, "E286.left", {"start": v(315.8, 221.55) * mm, "end": v(315.8, 234.25) * mm});
            skLineSegment(sketch, "E286.right", {"start": v(328.5, 221.55) * mm, "end": v(328.5, 234.25) * mm});
            skLineSegment(sketch, "E287.bottom", {"start": v(315.8, 259.65) * mm, "end": v(328.5, 259.65) * mm});
            skLineSegment(sketch, "E287.top", {"start": v(315.8, 272.35) * mm, "end": v(328.5, 272.35) * mm});
            skLineSegment(sketch, "E287.left", {"start": v(315.8, 259.65) * mm, "end": v(315.8, 272.35) * mm});
            skLineSegment(sketch, "E287.right", {"start": v(328.5, 259.65) * mm, "end": v(328.5, 272.35) * mm});
            skLineSegment(sketch, "E288.bottom", {"start": v(315.8, 297.75) * mm, "end": v(328.5, 297.75) * mm});
            skLineSegment(sketch, "E288.top", {"start": v(315.8, 310.45) * mm, "end": v(328.5, 310.45) * mm});
            skLineSegment(sketch, "E288.left", {"start": v(315.8, 297.75) * mm, "end": v(315.8, 310.45) * mm});
            skLineSegment(sketch, "E288.right", {"start": v(328.5, 297.75) * mm, "end": v(328.5, 310.45) * mm});
            skLineSegment(sketch, "E289.bottom", {"start": v(315.8, 335.85) * mm, "end": v(328.5, 335.85) * mm});
            skLineSegment(sketch, "E289.top", {"start": v(315.8, 348.55) * mm, "end": v(328.5, 348.55) * mm});
            skLineSegment(sketch, "E289.left", {"start": v(315.8, 335.85) * mm, "end": v(315.8, 348.55) * mm});
            skLineSegment(sketch, "E289.right", {"start": v(328.5, 335.85) * mm, "end": v(328.5, 348.55) * mm});
            skLineSegment(sketch, "E290", {"start": v(341.2, -7.05) * mm, "end": v(360.26, -7.05) * mm});
            skLineSegment(sketch, "E291", {"start": v(334.86, -7.05) * mm, "end": v(328.5, -7.05) * mm});
            skLineSegment(sketch, "E292", {"start": v(347.56, 399.35) * mm, "end": v(341.2, 399.35) * mm});
            skLineSegment(sketch, "E293", {"start": v(347.56, 424.75) * mm, "end": v(341.2, 424.75) * mm});
            skLineSegment(sketch, "E294", {"start": v(347.56, 475.55) * mm, "end": v(341.2, 475.55) * mm});
            skLineSegment(sketch, "E295", {"start": v(347.56, 500.95) * mm, "end": v(341.2, 500.95) * mm});
            skLineSegment(sketch, "E296", {"start": v(341.2, 424.75) * mm, "end": v(341.2, 399.35) * mm});
            skLineSegment(sketch, "E297", {"start": v(341.2, 500.95) * mm, "end": v(341.2, 475.55) * mm});
            skLineSegment(sketch, "E298", {"start": v(347.56, 500.95) * mm, "end": v(347.56, 475.55) * mm});
            skLineSegment(sketch, "E299", {"start": v(347.56, 424.75) * mm, "end": v(347.56, 399.35) * mm});
            skLineSegment(sketch, "E300", {"start": v(303.1, 399.35) * mm, "end": v(296.76, 399.35) * mm});
            skLineSegment(sketch, "E301", {"start": v(303.1, 424.75) * mm, "end": v(296.76, 424.75) * mm});
            skLineSegment(sketch, "E302", {"start": v(303.1, 475.55) * mm, "end": v(296.76, 475.55) * mm});
            skLineSegment(sketch, "E303", {"start": v(303.1, 500.95) * mm, "end": v(296.76, 500.95) * mm});
            skLineSegment(sketch, "E304", {"start": v(303.1, 500.95) * mm, "end": v(303.1, 475.55) * mm});
            skLineSegment(sketch, "E305", {"start": v(303.1, 424.75) * mm, "end": v(303.1, 399.35) * mm});
            skLineSegment(sketch, "E306", {"start": v(296.76, 348.55) * mm, "end": v(296.76, 399.35) * mm});
            skLineSegment(sketch, "E307", {"start": v(296.76, 424.75) * mm, "end": v(296.76, 475.55) * mm});
            skLineSegment(sketch, "E308.bottom", {"start": v(315.8, 373.95) * mm, "end": v(328.5, 373.95) * mm});
            skLineSegment(sketch, "E308.top", {"start": v(315.8, 386.65) * mm, "end": v(328.5, 386.65) * mm});
            skLineSegment(sketch, "E308.left", {"start": v(315.8, 373.95) * mm, "end": v(315.8, 386.65) * mm});
            skLineSegment(sketch, "E308.right", {"start": v(328.5, 373.95) * mm, "end": v(328.5, 386.65) * mm});
            skLineSegment(sketch, "E309.bottom", {"start": v(315.8, 412.05) * mm, "end": v(328.5, 412.05) * mm});
            skLineSegment(sketch, "E309.top", {"start": v(315.8, 424.75) * mm, "end": v(328.5, 424.75) * mm});
            skLineSegment(sketch, "E309.left", {"start": v(315.8, 412.05) * mm, "end": v(315.8, 424.75) * mm});
            skLineSegment(sketch, "E309.right", {"start": v(328.5, 412.05) * mm, "end": v(328.5, 424.75) * mm});
            skLineSegment(sketch, "E310.bottom", {"start": v(315.8, 450.15) * mm, "end": v(328.5, 450.15) * mm});
            skLineSegment(sketch, "E310.top", {"start": v(315.8, 462.85) * mm, "end": v(328.5, 462.85) * mm});
            skLineSegment(sketch, "E310.left", {"start": v(315.8, 450.15) * mm, "end": v(315.8, 462.85) * mm});
            skLineSegment(sketch, "E310.right", {"start": v(328.5, 450.15) * mm, "end": v(328.5, 462.85) * mm});
            skLineSegment(sketch, "E311.bottom", {"start": v(315.8, 488.25) * mm, "end": v(328.5, 488.25) * mm});
            skLineSegment(sketch, "E311.top", {"start": v(315.8, 500.95) * mm, "end": v(328.5, 500.95) * mm});
            skLineSegment(sketch, "E311.left", {"start": v(315.8, 488.25) * mm, "end": v(315.8, 500.95) * mm});
            skLineSegment(sketch, "E311.right", {"start": v(328.5, 488.25) * mm, "end": v(328.5, 500.95) * mm});
            skLineSegment(sketch, "E312", {"start": v(296.76, 500.95) * mm, "end": v(296.76, 526.35) * mm});
            skLineSegment(sketch, "E313", {"start": v(296.76, 526.35) * mm, "end": v(360.26, 526.35) * mm});
            skLineSegment(sketch, "E314", {"start": v(360.26, 526.35) * mm, "end": v(360.26, -7.05) * mm});
            skSolve(sketch);
        }
        {
            var Q0;
            Q0=makeQuery(id+"F10.imprint","IMPRINT",FACE,{"disambiguationData":[TD([[makeQuery(id+"F10.imprint","IMPRINT",EDGE,{"derivedFrom":sQuery(id+"F10.wireOp",EDGE,"E238")}),1.0]])]});
            extrude(context, id + "F11", {"entities" : qUnion([Q0]), "depth" : 6.35 * mm, "offsetDistance" : 25.4 * mm});
        }
    });
